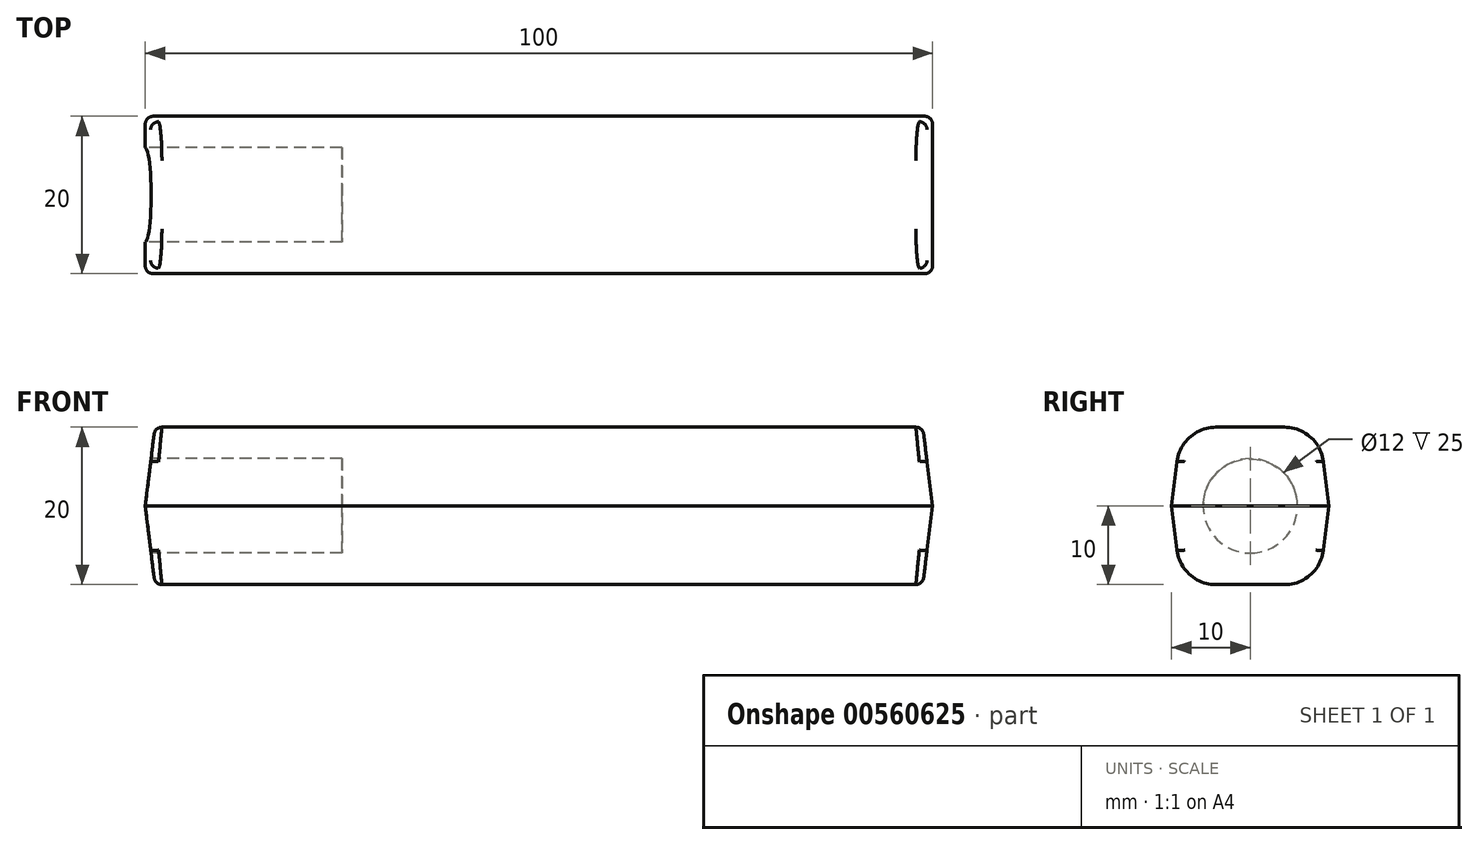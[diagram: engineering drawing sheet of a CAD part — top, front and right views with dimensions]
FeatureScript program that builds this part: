
annotation { "Feature Type Name" : "Feature", "Feature Type Description" : "" }
export const myFeature = defineFeature(function(context is Context, id is Id, definition is map)
    precondition{}
    {
        {
            var Q0;
            Q0=qCreatedBy(makeId("Top.planeOp"),FACE);
            var sketch = newSketch(context, id + "F0", { "sketchPlane" : qUnion([Q0])});
            skLineSegment(sketch, "E0.bottom", {"start": v(0, 0) * mm, "end": v(100, 0) * mm});
            skLineSegment(sketch, "E0.top", {"start": v(0, -20) * mm, "end": v(100, -20) * mm});
            skLineSegment(sketch, "E0.left", {"start": v(0, 0) * mm, "end": v(0, -20) * mm});
            skLineSegment(sketch, "E0.right", {"start": v(100, 0) * mm, "end": v(100, -20) * mm});
            skSolve(sketch);
        }
        {
            var Q0;
            Q0 = qSketchRegion(id + "F0", true);
            extrude(context, id + "F1", {"entities" : qUnion([Q0]), "endBound" : BoundingType.SYMMETRIC, "depth" : 20 * mm, "offsetDistance" : 25 * mm, "hasDraft" : true, "draftAngle" : 7 * degree, "draftPullDirection" : true});
        }
        {
            var Q0;
            Q0=makeQuery(id+"F1.opExtrude","CAP_EDGE",EDGE,{"disambiguationData":[OSD([sQuery(id+"F0.wireOp",EDGE,"E0.top")])],"isStart":false});
            var Q1;
            Q1=makeQuery(id+"F1.opExtrude","CAP_EDGE",EDGE,{"disambiguationData":[OSD([sQuery(id+"F0.wireOp",EDGE,"E0.bottom")])],"isStart":false});
            var Q2;
            Q2=makeQuery(id+"F1.opExtrude","CAP_EDGE",EDGE,{"disambiguationData":[OSD([sQuery(id+"F0.wireOp",EDGE,"E0.bottom")])],"isStart":true});
            var Q3;
            Q3=makeQuery(id+"F1.opExtrude","CAP_EDGE",EDGE,{"disambiguationData":[OSD([sQuery(id+"F0.wireOp",EDGE,"E0.top")])],"isStart":true});
            fillet(context, id + "F2", {"entities" : qUnion([Q0, Q1, Q2, Q3]), "radius" : 5 * mm, "tangentPropagation" : true, "allowEdgeOverflow" : false});
        }
        {
            var Q0;
            Q0=makeQuery(id+"F1.opExtrude","CAP_EDGE",EDGE,{"disambiguationData":[OSD([sQuery(id+"F0.wireOp",EDGE,"E0.right")])],"isStart":false});
            fillet(context, id + "F3", {"entities" : qUnion([Q0]), "radius" : 1 * mm, "tangentPropagation" : true, "allowEdgeOverflow" : false});
        }
        {
            var Q0;
            Q0=makeQuery(id+"F1.opExtrude","CAP_EDGE",EDGE,{"disambiguationData":[OSD([sQuery(id+"F0.wireOp",EDGE,"E0.left")])],"isStart":false});
            var Q1;
            Q1=makeQuery(id+"F1.opExtrude","CAP_EDGE",EDGE,{"disambiguationData":[OSD([sQuery(id+"F0.wireOp",EDGE,"E0.left")])],"isStart":true});
            var Q2;
            Q2=makeQuery(id+"F1.opExtrude","CAP_EDGE",EDGE,{"disambiguationData":[OSD([sQuery(id+"F0.wireOp",EDGE,"E0.right")])],"isStart":true});
            fillet(context, id + "F4", {"entities" : qUnion([Q0, Q1, Q2]), "radius" : 1 * mm, "tangentPropagation" : true, "allowEdgeOverflow" : false});
        }
        {
            var Q0;
            Q0=qCreatedBy(makeId("Right.planeOp"),FACE);
            var sketch = newSketch(context, id + "F5", { "sketchPlane" : qUnion([Q0])});
            skLineSegment(sketch, "E1", {"start": v(0, 0) * mm, "end": v(-10, 0) * mm});
            skCircle(sketch, "E2", {"center": v(-10, 0) * mm, "radius": 6 * mm});
            skSolve(sketch);
        }
        {
            var Q0;
            Q0 = qSketchRegion(id + "F5", true);
            extrude(context, id + "F6", {"entities" : qUnion([Q0]), "operationType" : NewBodyOperationType.REMOVE, "depth" : 25 * mm, "offsetDistance" : 25 * mm});
        }
    });
